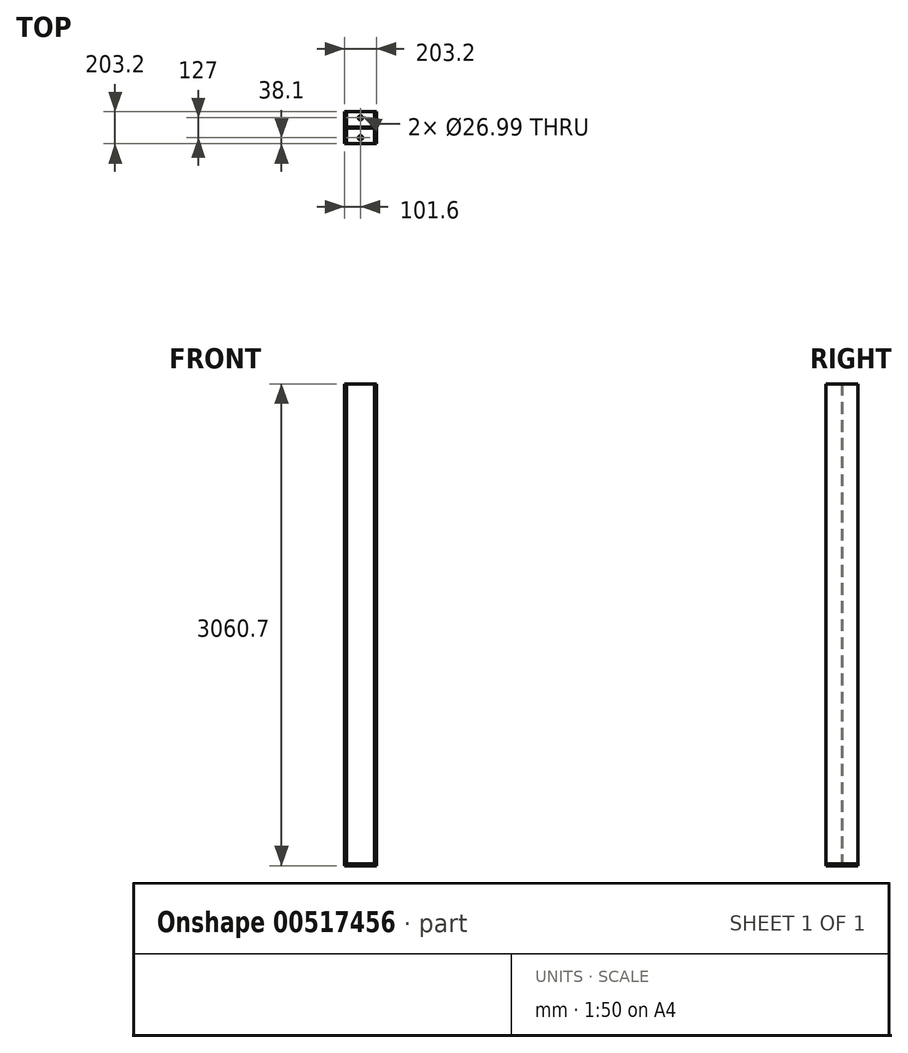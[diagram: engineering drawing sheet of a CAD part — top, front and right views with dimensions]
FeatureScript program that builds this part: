
annotation { "Feature Type Name" : "Feature", "Feature Type Description" : "" }
export const myFeature = defineFeature(function(context is Context, id is Id, definition is map)
    precondition{}
    {
        {
            var Q0;
            Q0=qCreatedBy(makeId("Top.planeOp"),FACE);
            var sketch = newSketch(context, id + "F0", { "sketchPlane" : qUnion([Q0])});
            skLineSegment(sketch, "E0.bottom", {"start": v(-101.6, 101.6) * mm, "end": v(101.6, 101.6) * mm});
            skLineSegment(sketch, "E0.top", {"start": v(-101.6, -101.6) * mm, "end": v(101.6, -101.6) * mm});
            skLineSegment(sketch, "E0.left", {"start": v(-101.6, 101.6) * mm, "end": v(-101.6, -101.6) * mm});
            skLineSegment(sketch, "E0.right", {"start": v(101.6, 101.6) * mm, "end": v(101.6, -101.6) * mm});
            skLineSegment(sketch, "E1", {"start": v(-101.6, 101.6) * mm, "end": v(101.6, -101.6) * mm, "construction": true});
            skCircle(sketch, "E2", {"center": v(0, -63.5) * mm, "radius": 13.5 * mm});
            skLineSegment(sketch, "E3", {"start": v(0, -63.5) * mm, "end": v(0, 63.5) * mm, "construction": true});
            skCircle(sketch, "E4", {"center": v(0, 63.5) * mm, "radius": 13.5 * mm});
            skSolve(sketch);
        }
        {
            var Q0;
            Q0=makeQuery(id+"F0.imprint","IMPRINT",FACE,{"disambiguationData":[TD([[makeQuery(id+"F0.imprint","IMPRINT",EDGE,{"derivedFrom":sQuery(id+"F0.wireOp",EDGE,"E0.bottom")}),-1.0]])]});
            extrude(context, id + "F1", {"entities" : qUnion([Q0]), "depth" : 12.7 * mm, "offsetDistance" : 25.4 * mm});
        }
        {
            var Q0;
            Q0=makeQuery(id+"F1.opExtrude","CAP_FACE",FACE,{"disambiguationData":[OSD([sQuery(id+"F0.wireOp",EDGE,"E0.bottom"),sQuery(id+"F0.wireOp",EDGE,"E0.top"),sQuery(id+"F0.wireOp",EDGE,"E0.left"),sQuery(id+"F0.wireOp",EDGE,"E0.right"),sQuery(id+"F0.wireOp",EDGE,"E2"),sQuery(id+"F0.wireOp",EDGE,"E4")])],"isStart":false});
            var sketch = newSketch(context, id + "F2", { "sketchPlane" : qUnion([Q0])});
            skLineSegment(sketch, "E5.bottom", {"start": v(-101.6, 101.6) * mm, "end": v(-88.9, 101.6) * mm});
            skLineSegment(sketch, "E5.top", {"start": v(-101.6, -101.6) * mm, "end": v(-88.9, -101.6) * mm});
            skLineSegment(sketch, "E5.left", {"start": v(-101.6, 101.6) * mm, "end": v(-101.6, -101.6) * mm});
            skLineSegment(sketch, "E5.right", {"start": v(-88.9, 101.6) * mm, "end": v(-88.9, 3.18) * mm});
            skLineSegment(sketch, "E6.bottom", {"start": v(88.9, 101.6) * mm, "end": v(101.6, 101.6) * mm});
            skLineSegment(sketch, "E6.top", {"start": v(88.9, -101.6) * mm, "end": v(101.6, -101.6) * mm});
            skLineSegment(sketch, "E6.left", {"start": v(88.9, 101.6) * mm, "end": v(88.9, 3.18) * mm});
            skLineSegment(sketch, "E6.right", {"start": v(101.6, 101.6) * mm, "end": v(101.6, -101.6) * mm});
            skLineSegment(sketch, "E7.top", {"start": v(-88.9, -3.17) * mm, "end": v(88.9, -3.17) * mm});
            skLineSegment(sketch, "E8", {"start": v(-88.9, 3.18) * mm, "end": v(88.9, 3.18) * mm});
            skLineSegment(sketch, "E9.trimOffspring", {"start": v(-88.9, -3.17) * mm, "end": v(-88.9, -101.6) * mm});
            skLineSegment(sketch, "E10.trimOffspring", {"start": v(88.9, -3.17) * mm, "end": v(88.9, -101.6) * mm});
            skLineSegment(sketch, "E11", {"start": v(-101.6, 101.6) * mm, "end": v(101.6, -101.6) * mm, "construction": true});
            skSolve(sketch);
        }
        {
            var Q0;
            Q0 = qSketchRegion(id + "F2", true);
            extrude(context, id + "F3", {"entities" : qUnion([Q0]), "depth" : 3048 * mm, "offsetDistance" : 25.4 * mm});
        }
    });
